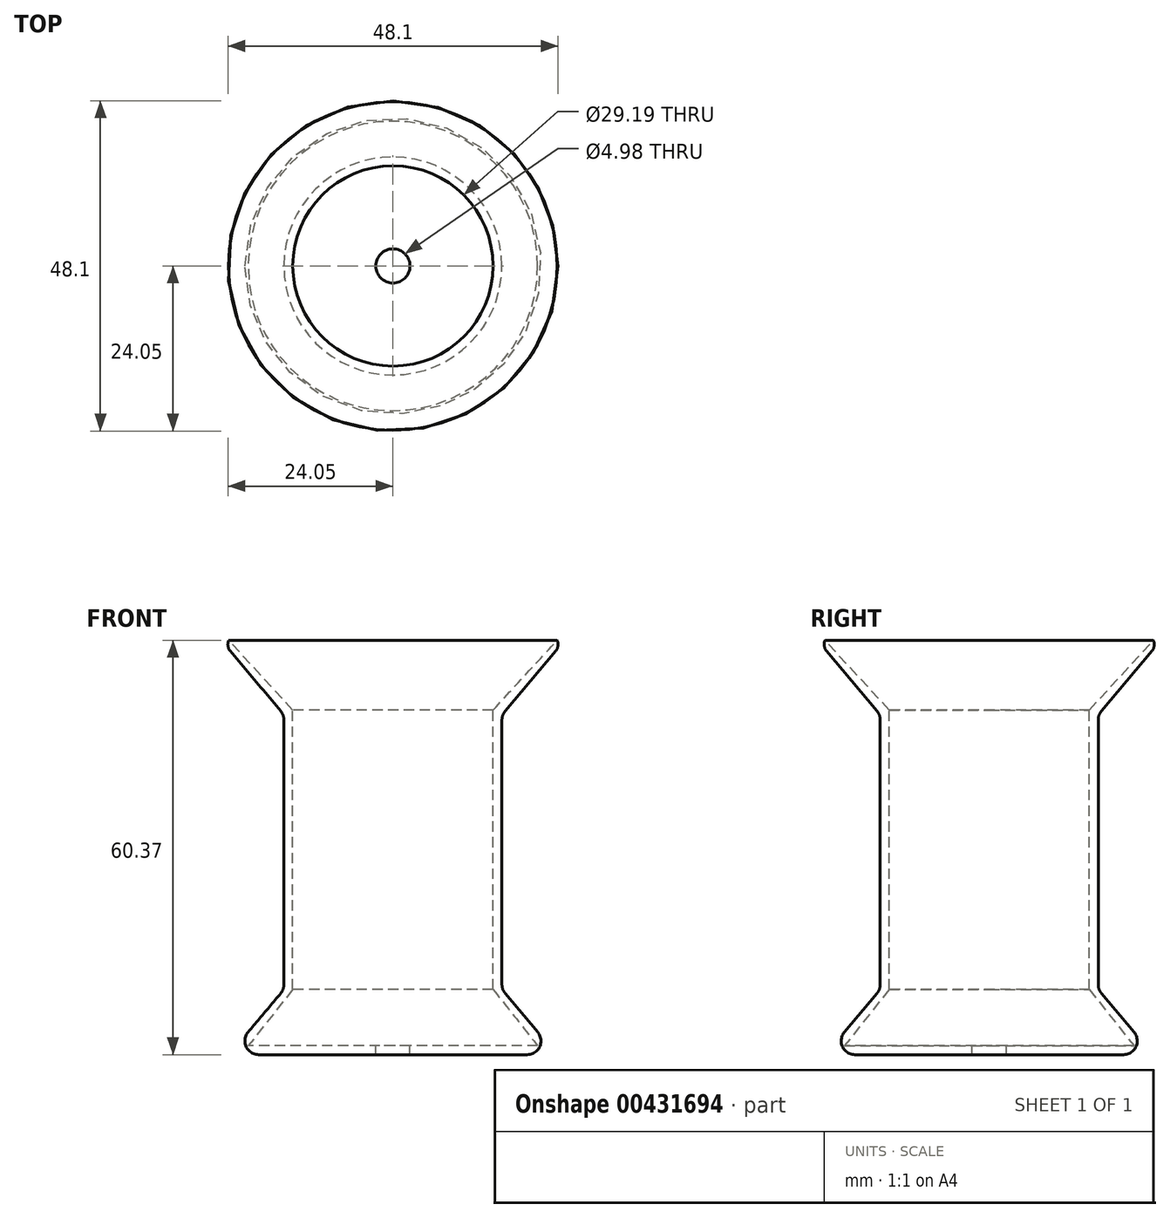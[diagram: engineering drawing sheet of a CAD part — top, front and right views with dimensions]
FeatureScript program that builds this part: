
annotation { "Feature Type Name" : "Feature", "Feature Type Description" : "" }
export const myFeature = defineFeature(function(context is Context, id is Id, definition is map)
    precondition{}
    {
        {
            var Q0;
            Q0=qCreatedBy(makeId("Front.planeOp"),FACE);
            var sketch = newSketch(context, id + "F0", { "sketchPlane" : qUnion([Q0])});
            skLineSegment(sketch, "E0", {"start": v(15.88, 0) * mm, "end": v(15.88, 20) * mm});
            skLineSegment(sketch, "E1", {"start": v(15.88, 20) * mm, "end": v(25, 30.87) * mm});
            skLineSegment(sketch, "E2", {"start": v(15.88, 0) * mm, "end": v(15.88, -20) * mm});
            skLineSegment(sketch, "E3", {"start": v(15.88, -20) * mm, "end": v(23.86, -29.5) * mm});
            skLineSegment(sketch, "E4", {"start": v(0, 30.87) * mm, "end": v(0, -30.87) * mm, "construction": true});
            skLineSegment(sketch, "E5.1", {"start": v(14.6, 20.73) * mm, "end": v(23.94, 30.87) * mm});
            skLineSegment(sketch, "E5.4", {"start": v(14.6, 0.36) * mm, "end": v(14.6, -20) * mm});
            skLineSegment(sketch, "E5.5", {"start": v(14.6, 0.36) * mm, "end": v(14.6, 20.73) * mm});
            skLineSegment(sketch, "E6", {"start": v(25, 30.87) * mm, "end": v(23.94, 30.87) * mm});
            skLineSegment(sketch, "E7", {"start": v(22.57, -29.5) * mm, "end": v(23.86, -29.5) * mm});
            skPoint(sketch, "E8", {"position": v(21.1, -28.21) * mm});
            skLineSegment(sketch, "E9", {"start": v(14.6, -20) * mm, "end": v(21.1, -28.21) * mm});
            skLineSegment(sketch, "E10", {"start": v(0, -28.21) * mm, "end": v(0, -29.5) * mm});
            skLineSegment(sketch, "E11", {"start": v(22.57, -29.5) * mm, "end": v(2.49, -29.5) * mm});
            skLineSegment(sketch, "E12", {"start": v(2.49, -29.5) * mm, "end": v(2.49, -28.21) * mm});
            skLineSegment(sketch, "E13", {"start": v(2.49, -28.21) * mm, "end": v(21.1, -28.21) * mm});
            skSolve(sketch);
        }
        {
            var Q0;
            Q0=makeQuery(id+"F0.imprint","IMPRINT",FACE,{"disambiguationData":[TD([[makeQuery(id+"F0.imprint","IMPRINT",EDGE,{"derivedFrom":sQuery(id+"F0.wireOp",EDGE,"E0")}),1.0]])]});
            var Q1;
            Q1=sQuery(id+"F0.wireOp",EDGE,"E4");
            revolve(context, id + "F1", {"entities" : qUnion([Q0]), "axis" : qUnion([Q1]), "revolveType" : RevolveType.FULL});
        }
        {
            var Q0;
            Q0=makeQuery(id+"F1.opRevolve","SWEPT_EDGE",EDGE,{"disambiguationData":[OSD([sQuery(id+"F0.wireOp",EDGE,"E2"),sQuery(id+"F0.wireOp",EDGE,"E3")])]});
            var Q1;
            Q1=makeQuery(id+"F1.opRevolve","SWEPT_EDGE",EDGE,{"disambiguationData":[OSD([sQuery(id+"F0.wireOp",EDGE,"E0"),sQuery(id+"F0.wireOp",EDGE,"E1")])]});
            var Q2;
            Q2=makeQuery(id+"F1.opRevolve","SWEPT_EDGE",EDGE,{"disambiguationData":[OSD([sQuery(id+"F0.wireOp",EDGE,"E3"),sQuery(id+"F0.wireOp",EDGE,"E7")])]});
            fillet(context, id + "F2", {"entities" : qUnion([Q0, Q1, Q2]), "radius" : 2 * mm, "tangentPropagation" : true, "allowEdgeOverflow" : false});
        }
        {
            var Q0;
            Q0=makeQuery(id+"F1.opRevolve","SWEPT_EDGE",EDGE,{"disambiguationData":[OSD([sQuery(id+"F0.wireOp",EDGE,"E1"),sQuery(id+"F0.wireOp",EDGE,"E6")])]});
            fillet(context, id + "F3", {"entities" : qUnion([Q0]), "radius" : 1.5 * mm, "tangentPropagation" : true, "allowEdgeOverflow" : false});
        }
    });
